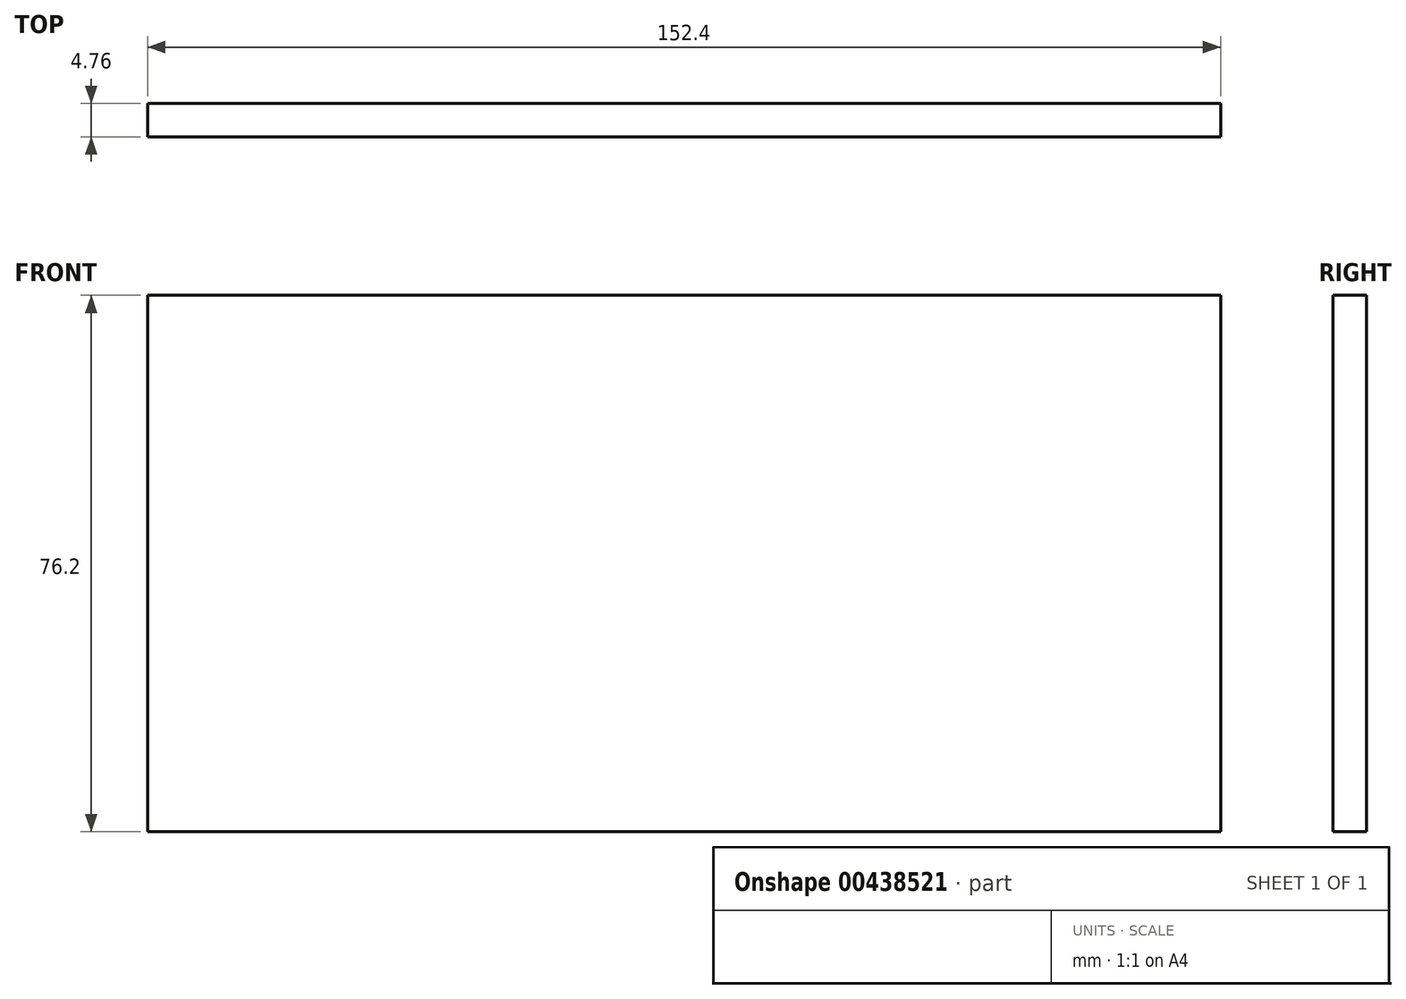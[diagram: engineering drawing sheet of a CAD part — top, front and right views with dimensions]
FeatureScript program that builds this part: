
annotation { "Feature Type Name" : "Feature", "Feature Type Description" : "" }
export const myFeature = defineFeature(function(context is Context, id is Id, definition is map)
    precondition{}
    {
        {
            var Q0;
            Q0=qCreatedBy(makeId("Front.planeOp"),FACE);
            var sketch = newSketch(context, id + "F0", { "sketchPlane" : qUnion([Q0])});
            skLineSegment(sketch, "E0.bottom", {"start": v(-82.47, -38.16) * mm, "end": v(69.93, -38.16) * mm});
            skLineSegment(sketch, "E0.top", {"start": v(-82.47, -114.36) * mm, "end": v(69.93, -114.36) * mm});
            skLineSegment(sketch, "E0.left", {"start": v(-82.47, -38.16) * mm, "end": v(-82.47, -114.36) * mm});
            skLineSegment(sketch, "E0.right", {"start": v(69.93, -38.16) * mm, "end": v(69.93, -114.36) * mm});
            skSolve(sketch);
        }
        {
            var Q0;
            Q0=makeQuery(id+"F0.imprint","IMPRINT",FACE,{"disambiguationData":[TD([[makeQuery(id+"F0.imprint","IMPRINT",EDGE,{"derivedFrom":sQuery(id+"F0.wireOp",EDGE,"E0.bottom")}),-1.0]])]});
            extrude(context, id + "F1", {"entities" : qUnion([Q0]), "depth" : 4.76 * mm});
        }
    });
